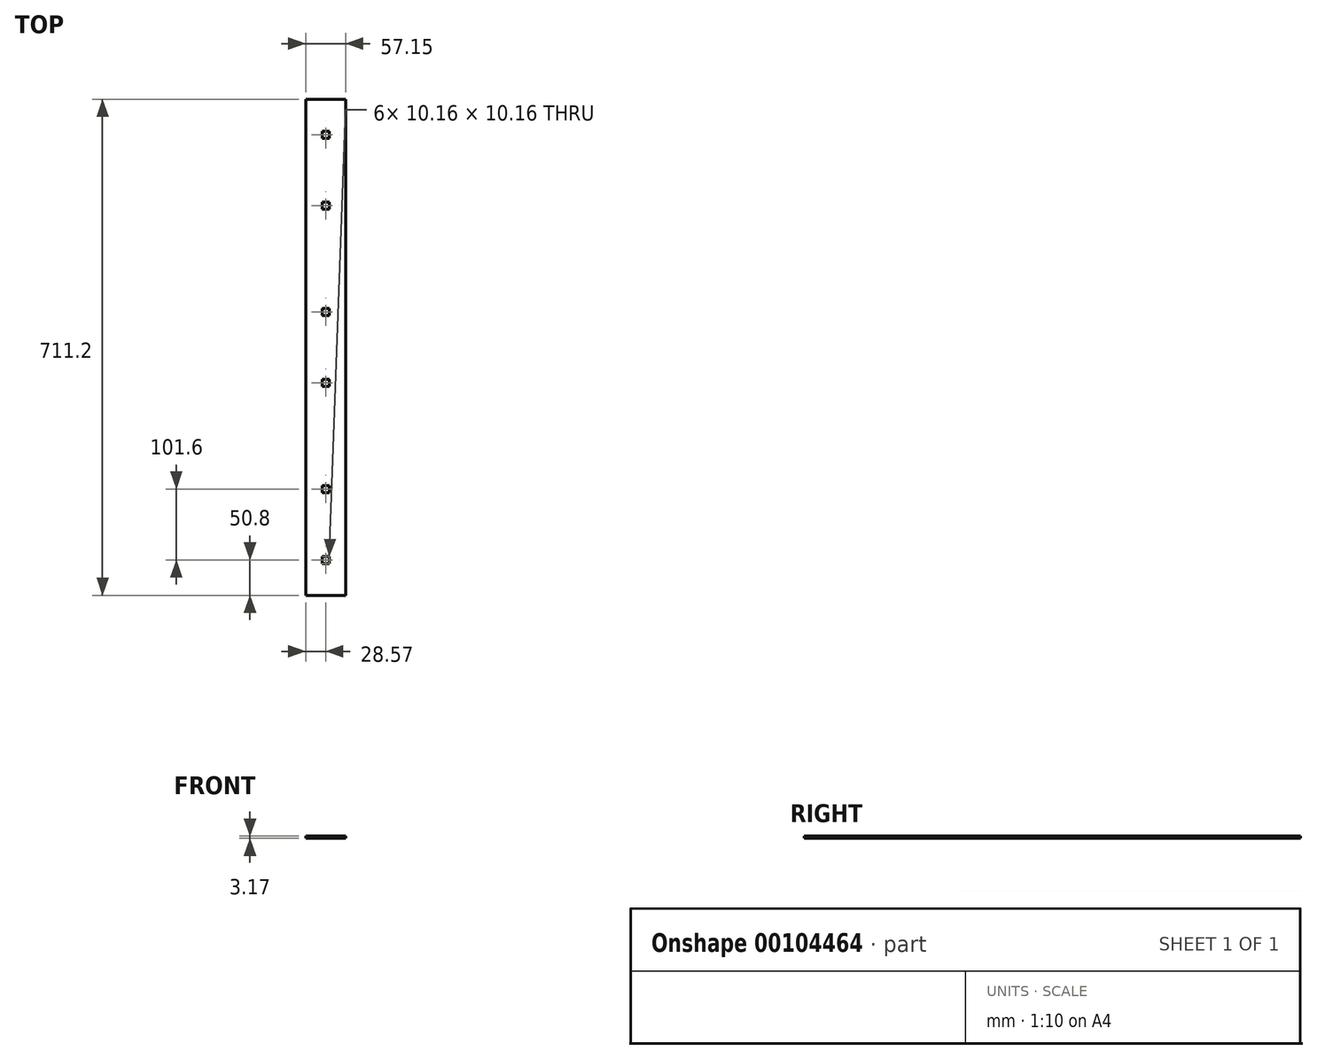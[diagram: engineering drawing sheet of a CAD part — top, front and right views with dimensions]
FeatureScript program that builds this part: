
annotation { "Feature Type Name" : "Feature", "Feature Type Description" : "" }
export const myFeature = defineFeature(function(context is Context, id is Id, definition is map)
    precondition{}
    {
        {
            var Q0;
            Q0=qCreatedBy(makeId("Top.planeOp"),FACE);
            var sketch = newSketch(context, id + "F0", { "sketchPlane" : qUnion([Q0])});
            skLineSegment(sketch, "E0.left", {"start": v(15.87, 25.4) * mm, "end": v(15.87, 736.6) * mm});
            skLineSegment(sketch, "E0.right", {"start": v(73.02, 25.4) * mm, "end": v(73.02, 736.6) * mm});
            skPoint(sketch, "E1.middle", {"position": v(44.45, 685.8) * mm});
            skPoint(sketch, "E2.middle", {"position": v(44.45, 584.2) * mm});
            skLineSegment(sketch, "E3.direction1", {"start": v(44.45, 584.2) * mm, "end": v(69.85, 584.2) * mm, "construction": true});
            skLineSegment(sketch, "E3.direction2", {"start": v(44.45, 584.2) * mm, "end": v(44.45, 330.2) * mm, "construction": true});
            skLineSegment(sketch, "E4.bottom", {"start": v(49.53, 690.88) * mm, "end": v(39.37, 690.88) * mm});
            skLineSegment(sketch, "E4.top", {"start": v(49.53, 680.72) * mm, "end": v(39.37, 680.72) * mm});
            skLineSegment(sketch, "E4.left", {"start": v(49.53, 690.88) * mm, "end": v(49.53, 680.72) * mm});
            skLineSegment(sketch, "E4.right", {"start": v(39.37, 690.88) * mm, "end": v(39.37, 680.72) * mm});
            skLineSegment(sketch, "E5.bottom", {"start": v(49.53, 589.28) * mm, "end": v(39.37, 589.28) * mm});
            skLineSegment(sketch, "E5.top", {"start": v(49.53, 579.12) * mm, "end": v(39.37, 579.12) * mm});
            skLineSegment(sketch, "E5.left", {"start": v(49.53, 589.28) * mm, "end": v(49.53, 579.12) * mm});
            skLineSegment(sketch, "E5.right", {"start": v(39.37, 589.28) * mm, "end": v(39.37, 579.12) * mm});
            skLineSegment(sketch, "E6.0.1.0", {"start": v(49.53, 436.88) * mm, "end": v(39.37, 436.88) * mm});
            skPoint(sketch, "E6.0.1.1", {"position": v(44.45, 330.2) * mm});
            skPoint(sketch, "E6.0.1.2", {"position": v(44.45, 431.8) * mm});
            skLineSegment(sketch, "E6.0.1.3", {"start": v(49.53, 335.28) * mm, "end": v(49.53, 325.12) * mm});
            skLineSegment(sketch, "E6.0.1.4", {"start": v(49.53, 335.28) * mm, "end": v(39.37, 335.28) * mm});
            skLineSegment(sketch, "E6.0.1.5", {"start": v(39.37, 436.88) * mm, "end": v(39.37, 426.72) * mm});
            skLineSegment(sketch, "E6.0.1.6", {"start": v(49.53, 436.88) * mm, "end": v(49.53, 426.72) * mm});
            skLineSegment(sketch, "E6.0.1.7", {"start": v(49.53, 426.72) * mm, "end": v(39.37, 426.72) * mm});
            skPoint(sketch, "E6.0.1.8", {"position": v(44.45, 431.8) * mm});
            skPoint(sketch, "E6.0.1.9", {"position": v(44.45, 330.2) * mm});
            skLineSegment(sketch, "E6.0.1.10", {"start": v(39.37, 335.28) * mm, "end": v(39.37, 325.12) * mm});
            skLineSegment(sketch, "E6.0.1.11", {"start": v(49.53, 325.12) * mm, "end": v(39.37, 325.12) * mm});
            skLineSegment(sketch, "E6.0.2.0", {"start": v(49.53, 182.88) * mm, "end": v(39.37, 182.88) * mm});
            skPoint(sketch, "E6.0.2.1", {"position": v(44.45, 76.2) * mm});
            skPoint(sketch, "E6.0.2.2", {"position": v(44.45, 177.8) * mm});
            skLineSegment(sketch, "E6.0.2.3", {"start": v(49.53, 81.28) * mm, "end": v(49.53, 71.12) * mm});
            skLineSegment(sketch, "E6.0.2.4", {"start": v(49.53, 81.28) * mm, "end": v(39.37, 81.28) * mm});
            skLineSegment(sketch, "E6.0.2.5", {"start": v(39.37, 182.88) * mm, "end": v(39.37, 172.72) * mm});
            skLineSegment(sketch, "E6.0.2.6", {"start": v(49.53, 182.88) * mm, "end": v(49.53, 172.72) * mm});
            skLineSegment(sketch, "E6.0.2.7", {"start": v(49.53, 172.72) * mm, "end": v(39.37, 172.72) * mm});
            skPoint(sketch, "E6.0.2.8", {"position": v(44.45, 177.8) * mm});
            skPoint(sketch, "E6.0.2.9", {"position": v(44.45, 76.2) * mm});
            skLineSegment(sketch, "E6.0.2.10", {"start": v(39.37, 81.28) * mm, "end": v(39.37, 71.12) * mm});
            skLineSegment(sketch, "E6.0.2.11", {"start": v(49.53, 71.12) * mm, "end": v(39.37, 71.12) * mm});
            skLineSegment(sketch, "E6.direction1", {"start": v(39.37, 579.12) * mm, "end": v(62.23, 579.12) * mm, "construction": true});
            skLineSegment(sketch, "E6.direction2", {"start": v(39.37, 579.12) * mm, "end": v(39.37, 325.12) * mm, "construction": true});
            skLineSegment(sketch, "E7", {"start": v(15.87, 736.6) * mm, "end": v(73.02, 736.6) * mm});
            skLineSegment(sketch, "E8", {"start": v(73.02, 25.4) * mm, "end": v(15.87, 25.4) * mm});
            skSolve(sketch);
        }
        {
            var Q0;
            Q0 = qSketchRegion(id + "F0", true);
            extrude(context, id + "F1", {"entities" : qUnion([Q0]), "depth" : 3.17 * mm});
        }
    });
